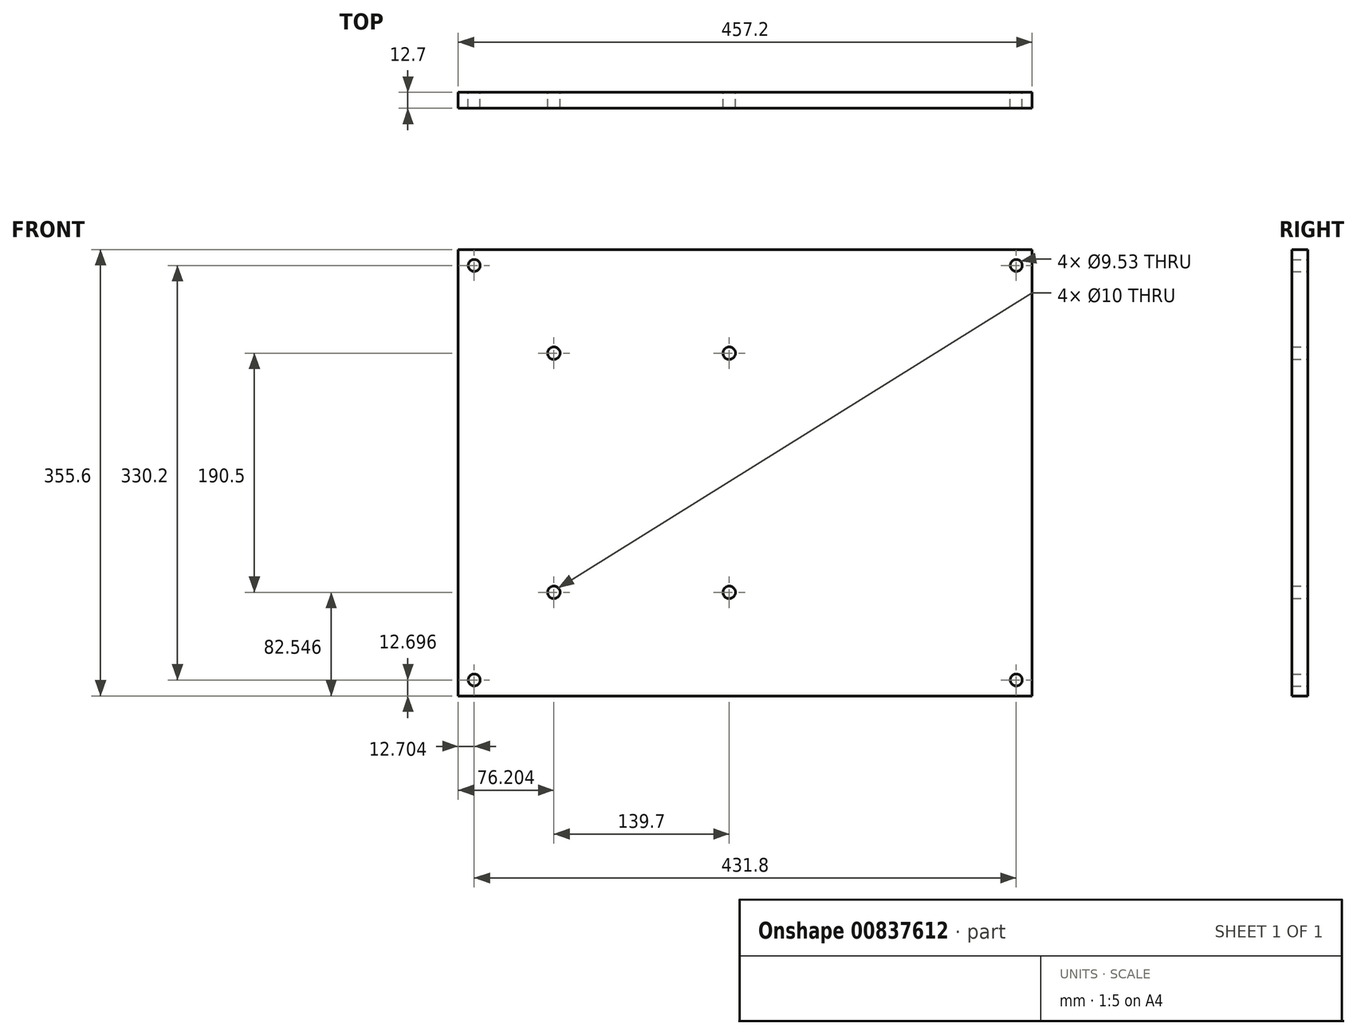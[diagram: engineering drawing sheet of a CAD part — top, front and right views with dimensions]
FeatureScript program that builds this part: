
annotation { "Feature Type Name" : "Feature", "Feature Type Description" : "" }
export const myFeature = defineFeature(function(context is Context, id is Id, definition is map)
    precondition{}
    {
        {
            var Q0;
            Q0=qCreatedBy(makeId("Front.planeOp"),FACE);
            var sketch = newSketch(context, id + "F0", { "sketchPlane" : qUnion([Q0])});
            skLineSegment(sketch, "E0.bottom", {"start": v(-202.87, -117.73) * mm, "end": v(254.33, -117.73) * mm});
            skLineSegment(sketch, "E0.top", {"start": v(-202.87, 237.87) * mm, "end": v(254.33, 237.87) * mm});
            skLineSegment(sketch, "E0.left", {"start": v(-202.87, -117.73) * mm, "end": v(-202.87, 237.87) * mm});
            skLineSegment(sketch, "E0.right", {"start": v(254.33, -117.73) * mm, "end": v(254.33, 237.87) * mm});
            skCircle(sketch, "E1", {"center": v(-126.67, -35.18) * mm, "radius": 5 * mm});
            skCircle(sketch, "E2", {"center": v(13.03, -35.18) * mm, "radius": 5 * mm});
            skCircle(sketch, "E3", {"center": v(-126.67, 155.32) * mm, "radius": 5 * mm});
            skCircle(sketch, "E4", {"center": v(13.03, 155.32) * mm, "radius": 5 * mm});
            skLineSegment(sketch, "E5", {"start": v(-202.87, 60.07) * mm, "end": v(254.33, 60.07) * mm, "construction": true});
            skLineSegment(sketch, "E6", {"start": v(-126.67, 155.32) * mm, "end": v(13.03, 155.32) * mm, "construction": true});
            skLineSegment(sketch, "E7", {"start": v(13.03, -35.18) * mm, "end": v(-126.67, -35.18) * mm, "construction": true});
            skLineSegment(sketch, "E8", {"start": v(-126.67, -35.18) * mm, "end": v(-126.67, 155.32) * mm, "construction": true});
            skLineSegment(sketch, "E9", {"start": v(13.03, 155.32) * mm, "end": v(13.03, -35.18) * mm, "construction": true});
            skLineSegment(sketch, "E10", {"start": v(-126.67, 60.07) * mm, "end": v(13.03, 60.07) * mm, "construction": true});
            skLineSegment(sketch, "E11", {"start": v(-56.82, 155.32) * mm, "end": v(-56.82, -35.18) * mm, "construction": true});
            skCircle(sketch, "E12", {"center": v(-190.17, 225.17) * mm, "radius": 4.76 * mm});
            skCircle(sketch, "E13", {"center": v(241.63, 225.17) * mm, "radius": 4.76 * mm});
            skCircle(sketch, "E14", {"center": v(241.63, -105.03) * mm, "radius": 4.76 * mm});
            skCircle(sketch, "E15", {"center": v(-190.17, -105.03) * mm, "radius": 4.76 * mm});
            skLineSegment(sketch, "E16", {"start": v(25.73, 237.87) * mm, "end": v(25.73, -117.73) * mm, "construction": true});
            skSolve(sketch);
        }
        {
            var Q0;
            Q0=makeQuery(id+"F0.imprint","IMPRINT",FACE,{"disambiguationData":[TD([[makeQuery(id+"F0.imprint","IMPRINT",EDGE,{"derivedFrom":sQuery(id+"F0.wireOp",EDGE,"E0.bottom")}),1.0]])]});
            extrude(context, id + "F1", {"entities" : qUnion([Q0]), "depth" : 12.7 * mm, "offsetDistance" : 25.4 * mm});
        }
    });
